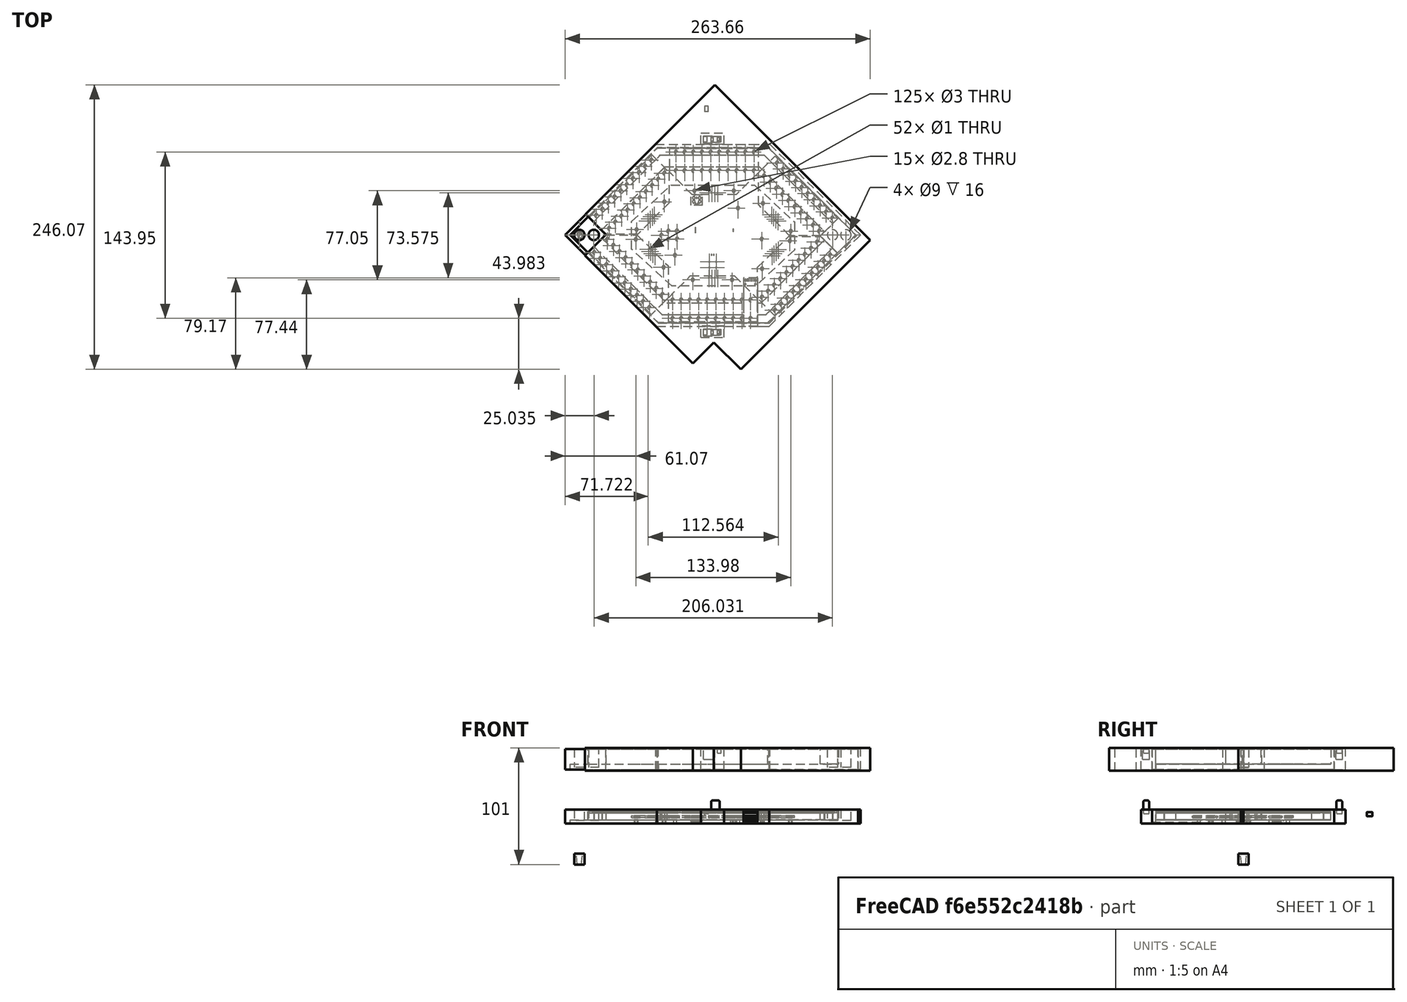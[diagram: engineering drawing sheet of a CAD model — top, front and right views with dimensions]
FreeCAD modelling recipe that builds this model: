
FCSTD DOCUMENT  (FreeCAD 1.0R39109 (Git))
Label: CribbageCase
License: All rights reserved
LicenseURL: https://en.wikipedia.org/wiki/All_rights_reserved
objects: Part::Box×49, Part::Cylinder×25, Part::MultiFuse×12, Part::Cut×8, Part::Feature×7, App::Part×3, Part::Fillet×2, Assembly::JointGroup×1, Mesh::Feature×1, Assembly::AssemblyObject×1, Part::Cone×1
note: 104 computed .brp shape members not serialized (recipe doc carries the construction recipe); baked Part::Feature solids carry a one-line shape summary decoded from their .brp

FEATURE [Assembly::JointGroup] Joints
FEATURE [Part::Feature] Part__Feature  label="MainBoard_PCB"
  shape: bbox 140.8 x 87.5 x 1.6 mm, 105 faces (baked)
FEATURE [Part::Cylinder] Cylinder  label="Screw00"
  Angle = 360
  AttacherType = Attacher::AttachEngine3D
  FirstAngle = 0
  Height = 20
  Placement = pos=(127.1,-56.28,-5) rot=(0,0,1;0rad)
  Radius = 1.4
  SecondAngle = 0
FEATURE [Part::Cylinder] Cylinder001  label="Screw01"
  Angle = 360
  AttacherType = Attacher::AttachEngine3D
  FirstAngle = 0
  Height = 20
  Placement = pos=(161.1,-56.28,-5) rot=(0,0,1;0rad)
  Radius = 1.4
  SecondAngle = 0
FEATURE [Part::Cylinder] Cylinder002  label="Screw03"
  Angle = 360
  AttacherType = Attacher::AttachEngine3D
  FirstAngle = 0
  Height = 20
  Placement = pos=(125.6,-133.33,-5) rot=(0,0,1;0rad)
  Radius = 1.4
  SecondAngle = 0
FEATURE [Part::Cylinder] Cylinder003  label="Screw04"
  Angle = 360
  AttacherType = Attacher::AttachEngine3D
  FirstAngle = 0
  Height = 20
  Placement = pos=(159.6,-133.33,-5) rot=(0,0,1;0rad)
  Radius = 1.4
  SecondAngle = 0
FEATURE [Part::Cylinder] Cylinder004  label="Screw08"
  Angle = 360
  AttacherType = Attacher::AttachEngine3D
  FirstAngle = 0
  Height = 20
  Placement = pos=(100.41,-122.46,-5) rot=(0,0,1;0rad)
  Radius = 1.4
  SecondAngle = 0
FEATURE [Part::Cylinder] Cylinder005  label="Screw02"
  Angle = 360
  AttacherType = Attacher::AttachEngine3D
  FirstAngle = 0
  Height = 20
  Placement = pos=(76.36,-98.41,-5) rot=(0,0,1;0rad)
  Radius = 1.4
  SecondAngle = 0
FEATURE [Part::Cylinder] Cylinder006  label="Screw05"
  Angle = 360
  AttacherType = Attacher::AttachEngine3D
  FirstAngle = 0
  Height = 20
  Placement = pos=(77.02,-89.89,-5) rot=(0,0,1;0rad)
  Radius = 1.4
  SecondAngle = 0
FEATURE [Part::Cylinder] Cylinder007  label="Screw06"
  Angle = 360
  AttacherType = Attacher::AttachEngine3D
  FirstAngle = 0
  Height = 20
  Placement = pos=(210.34,-91.24,-5) rot=(0,0,1;0rad)
  Radius = 1.4
  SecondAngle = 0
FEATURE [Part::Cylinder] Cylinder008  label="Screw07"
  Angle = 360
  AttacherType = Attacher::AttachEngine3D
  FirstAngle = 0
  Height = 20
  Placement = pos=(209.56,-99.67,-5) rot=(0,0,1;0rad)
  Radius = 1.4
  SecondAngle = 0
FEATURE [Part::Cylinder] Cylinder009  label="Screw09"
  Angle = 360
  AttacherType = Attacher::AttachEngine3D
  FirstAngle = 0
  Height = 20
  Placement = pos=(185.52,-123.71,-5) rot=(0,0,1;0rad)
  Radius = 1.4
  SecondAngle = 0
FEATURE [Part::Cylinder] Cylinder010  label="Screw11"
  Angle = 360
  AttacherType = Attacher::AttachEngine3D
  FirstAngle = 0
  Height = 20
  Placement = pos=(186.29,-67.2,-5) rot=(0,0,1;0rad)
  Radius = 1.4
  SecondAngle = 0
FEATURE [Part::Cylinder] Cylinder011  label="Screw10"
  Angle = 360
  AttacherType = Attacher::AttachEngine3D
  FirstAngle = 0
  Height = 20
  Placement = pos=(101.06,-65.84,-5) rot=(0,0,1;0rad)
  Radius = 1.4
  SecondAngle = 0
FEATURE [Part::Cylinder] Cylinder012  label="Screw12"
  Angle = 360
  AttacherType = Attacher::AttachEngine3D
  FirstAngle = 0
  Height = 20
  Placement = pos=(110.25,-112.03,-5) rot=(0,0,1;0rad)
  Radius = 1.4
  SecondAngle = 0
FEATURE [Part::Cylinder] Cylinder013  label="Screw14"
  Angle = 360
  AttacherType = Attacher::AttachEngine3D
  FirstAngle = 0
  Height = 20
  Placement = pos=(185.25,-98.03,-5) rot=(0,0,1;0rad)
  Radius = 1.4
  SecondAngle = 0
FEATURE [Part::Cylinder] Cylinder014  label="Screw13"
  Angle = 360
  AttacherType = Attacher::AttachEngine3D
  FirstAngle = 0
  Height = 20
  Placement = pos=(164.75,-71.28,-5) rot=(0,0,1;0rad)
  Radius = 1.4
  SecondAngle = 0
FEATURE [Part::Box] Box  label="USBCutout"
  AttacherType = Attacher::AttachEngine3D
  Height = 14.5
  Length = 12
  Placement = pos=(181.6,-131.77,-4) rot=(0,0,1;3.14159rad)
  Width = 45
FEATURE [Part::Box] Box001  label="JtagCutout"
  AttacherType = Attacher::AttachEngine3D
  Height = 3
  Length = 10
  Placement = pos=(124,-69,-3) rot=(0,0,1;0rad)
  Width = 9
FEATURE [Part::Feature] Part__Feature007  label="SensorBoard_0"
  Placement = pos=(-50.6,142.4,4) rot=(0,0,1;5.49779rad)
  shape: bbox 68.94 x 68.59 x 1.6 mm, 40 faces (baked)
FEATURE [Part::Feature] Part__Feature008  label="SensorBoard_1"
  Placement = pos=(201.1,198.225,4) rot=(0,0,1;4.71239rad)
  shape: bbox 76.5 x 40 x 1.6 mm, 40 faces (baked)
FEATURE [Part::Feature] Part__Feature009  label="SensorBoard_2"
  Placement = pos=(-131.9,-250.08,4) rot=(0,0,1;0.785398rad)
  shape: bbox 68.59 x 68.94 x 1.6 mm, 40 faces (baked)
FEATURE [Part::Feature] Part__Feature010  label="SensorBoard_3"
  Placement = pos=(85.6,-387.85,4) rot=(0,0,1;1.5708rad)
  shape: bbox 76.5 x 40 x 1.6 mm, 40 faces (baked)
FEATURE [Part::Feature] Part__Feature011  label="SensorBoard_4"
  Placement = pos=(337.2,-331.95,4) rot=(0,0,1;2.35619rad)
  shape: bbox 68.94 x 68.59 x 1.6 mm, 40 faces (baked)
FEATURE [Part::Feature] Part__Feature012  label="SensorBoard_5"
  Placement = pos=(418.58,60.44,4) rot=(0,0,1;3.92699rad)
  shape: bbox 68.59 x 68.94 x 1.6 mm, 40 faces (baked)
FEATURE [App::Part] MainBoard_1  label="Boards"
  Group = -> [Part__Feature,Part__Feature007,Part__Feature008,Part__Feature009,Part__Feature010,Part__Feature011,Part__Feature012]
  Origin = -> Origin001
FEATURE [Part::Box] Box002  label="Baseplate_0"
  AttacherType = Attacher::AttachEngine3D
  Height = 3
  Length = 140.75
  Placement = pos=(72.7,-138.81,-5) rot=(0,0,1;0rad)
  Width = 87.5
FEATURE [Part::Box] Box003  label="Baseplate_001"
  AttacherType = Attacher::AttachEngine3D
  Height = 3
  Length = 107.75
  Placement = pos=(19.53,-94.432,-5) rot=(0,0,1;5.49779rad)
  Width = 106.5
FEATURE [Part::Box] Box004  label="Baseplate_002"
  AttacherType = Attacher::AttachEngine3D
  Height = 3
  Length = 106.75
  Placement = pos=(116.44,-95.14,-5) rot=(0,0,1;5.49779rad)
  Width = 106.5
FEATURE [Part::Box] Box005  label="Baseplate_003"
  AttacherType = Attacher::AttachEngine3D
  Height = 3
  Length = 96.2
  Placement = pos=(95.72,-170.62,-5) rot=(0,0,1;0rad)
  Width = 75
FEATURE [Part::Box] Box006  label="Corner0"
  AttacherType = Attacher::AttachEngine3D
  Height = 9
  Length = 21.9
  Placement = pos=(19.5277,-94.4341,-2) rot=(0,0,1;5.49779rad)
  Width = 22.3
FEATURE [Part::Box] Box007  label="Edge00"
  AttacherType = Attacher::AttachEngine3D
  Height = 12
  Length = 3
  Placement = pos=(17.4063,-92.3128,-4.99) rot=(0,0,1;5.49779rad)
  Width = 107.685
FEATURE [Part::Box] Box008  label="Corner001"
  AttacherType = Attacher::AttachEngine3D
  Height = 9
  Length = 22
  Placement = pos=(267.227,-95.3109,-2) rot=(0,0,-1;3.92699rad)
  Width = 22.2
FEATURE [Part::Box] Box009  label="Support0"
  AttacherType = Attacher::AttachEngine3D
  Height = 6.4
  Length = 10
  Placement = pos=(182.092,-156.207,-2) rot=(0,0,1;5.49779rad)
  Width = 82
FEATURE [Part::Box] Box010  label="Support1"
  AttacherType = Attacher::AttachEngine3D
  Height = 6.4
  Length = 10
  Placement = pos=(98.7721,-153.45,-2) rot=(0,0,-1;1.5708rad)
  Width = 90.4
FEATURE [Part::Box] Box011  label="Support2"
  AttacherType = Attacher::AttachEngine3D
  Height = 6.4
  Length = 85
  Placement = pos=(180.232,-32.4421,-2) rot=(0,0,1;5.49779rad)
  Width = 10
FEATURE [Part::Box] Box012  label="Support3"
  AttacherType = Attacher::AttachEngine3D
  Height = 6.4
  Length = 10
  Placement = pos=(97.5326,-25.4286,-2) rot=(0,0,-1;1.5708rad)
  Width = 89.8
FEATURE [Part::Box] Box013  label="Support4"
  AttacherType = Attacher::AttachEngine3D
  Height = 6.4
  Length = 10
  Placement = pos=(46.4275,-96.8312,-2) rot=(0,0,1;3.92699rad)
  Width = 84
FEATURE [Part::Box] Box014  label="Support5"
  AttacherType = Attacher::AttachEngine3D
  Height = 6.4
  Length = 10
  Placement = pos=(39.2701,-83.7002,-2) rot=(0,0,1;5.49779rad)
  Width = 82.5
FEATURE [Part::Box] Box015  label="Edge001"
  AttacherType = Attacher::AttachEngine3D
  Height = 12
  Length = 3
  Placement = pos=(17.4063,-92.3128,-4.99) rot=(0,0,-1;2.35619rad)
  Width = 112
FEATURE [Part::Box] Box016  label="Edge002"
  AttacherType = Attacher::AttachEngine3D
  Height = 12
  Length = 3
  Placement = pos=(93.552,-16.1678,-4.99) rot=(0,0,-1;1.5708rad)
  Width = 98.75
FEATURE [Part::Box] Box017  label="Edge003"
  AttacherType = Attacher::AttachEngine3D
  Height = 12
  Length = 3
  Placement = pos=(94.492,-170.584,-4.99) rot=(0,0,-1;1.5708rad)
  Width = 97.2
FEATURE [Part::Box] Box018  label="Edge004"
  AttacherType = Attacher::AttachEngine3D
  Height = 12
  Length = 3
  Placement = pos=(189.569,-171.473,-4.99) rot=(0,0,-1;0.785398rad)
  Width = 109
FEATURE [Part::Box] Box019  label="Edge005"
  AttacherType = Attacher::AttachEngine3D
  Height = 12
  Length = 3
  Placement = pos=(192.298,-16.164,-4.99) rot=(0,0,1;3.92699rad)
  Width = 110.9
FEATURE [Part::Box] Box020  label="Baseplate_004"
  AttacherType = Attacher::AttachEngine3D
  Height = 3
  Length = 97.2
  Placement = pos=(94.85,-94.15,-5) rot=(0,0,1;0rad)
  Width = 75
FEATURE [App::Part] Part  label="BottomPlastics"
  Origin = -> Origin002
FEATURE [App::Part] Part001  label="TopPlastics"
  Origin = -> Origin003
FEATURE [Part::Box] Box021  label="Baseplate_005"
  AttacherType = Attacher::AttachEngine3D
  Height = 5
  Length = 97.2
  Placement = pos=(94.85,-94.15,-5) rot=(0,0,1;0rad)
  Width = 75
FEATURE [Part::Box] Box022  label="Baseplate_006"
  AttacherType = Attacher::AttachEngine3D
  Height = 5
  Length = 107.75
  Placement = pos=(19.53,-94.432,-5) rot=(0,0,1;5.49779rad)
  Width = 106.5
FEATURE [Part::Box] Box023  label="Baseplate_007"
  AttacherType = Attacher::AttachEngine3D
  Height = 5
  Length = 140.75
  Placement = pos=(72.7,-138.81,-5) rot=(0,0,1;0rad)
  Width = 87.5
FEATURE [Part::Box] Box024  label="Baseplate_008"
  AttacherType = Attacher::AttachEngine3D
  Height = 5
  Length = 106.75
  Placement = pos=(116.44,-95.14,-5) rot=(0,0,1;5.49779rad)
  Width = 106.5
FEATURE [Part::Box] Box025  label="Baseplate_009"
  AttacherType = Attacher::AttachEngine3D
  Height = 5
  Length = 96.2
  Placement = pos=(95.72,-170.62,-5) rot=(0,0,1;0rad)
  Width = 75
FEATURE [Part::Box] Box026  label="Edge006"
  AttacherType = Attacher::AttachEngine3D
  Height = 18
  Length = 3
  Placement = pos=(17.4063,-92.3128,-4.99) rot=(0,0,1;5.49779rad)
  Width = 107.685
FEATURE [Part::Box] Box027  label="Edge007"
  AttacherType = Attacher::AttachEngine3D
  Height = 18
  Length = 3
  Placement = pos=(17.4063,-92.3128,-4.99) rot=(0,0,-1;2.35619rad)
  Width = 112
FEATURE [Part::Box] Box028  label="Edge008"
  AttacherType = Attacher::AttachEngine3D
  Height = 18
  Length = 3
  Placement = pos=(93.552,-16.1678,-4.99) rot=(0,0,-1;1.5708rad)
  Width = 98.75
FEATURE [Part::Box] Box029  label="Edge009"
  AttacherType = Attacher::AttachEngine3D
  Height = 18
  Length = 3
  Placement = pos=(94.492,-170.584,-4.99) rot=(0,0,-1;1.5708rad)
  Width = 97.2
FEATURE [Part::Box] Box030  label="Edge010"
  AttacherType = Attacher::AttachEngine3D
  Height = 18
  Length = 3
  Placement = pos=(189.569,-171.473,-4.99) rot=(0,0,-1;0.785398rad)
  Width = 109
FEATURE [Part::Box] Box031  label="Edge011"
  AttacherType = Attacher::AttachEngine3D
  Height = 18
  Length = 3
  Placement = pos=(192.298,-16.164,-4.99) rot=(0,0,1;3.92699rad)
  Width = 110.9
FEATURE [Part::Box] Box032  label="Corner002"
  AttacherType = Attacher::AttachEngine3D
  Height = 13
  Length = 21.9
  Placement = pos=(19.5277,-94.4341,0) rot=(0,0,1;5.49779rad)
  Width = 22.3
FEATURE [Part::Box] Box033  label="Corner003"
  AttacherType = Attacher::AttachEngine3D
  Height = 13
  Length = 22
  Placement = pos=(267.227,-95.3109,0) rot=(0,0,-1;3.92699rad)
  Width = 22.2
FEATURE [Part::MultiFuse] Fusion002
  Placement = pos=(0,0,46.5) rot=(0,0,1;0rad)
  Shapes = -> [Box021,Box022,Box023,Box024,Box025,Box026,Box027,Box028,Box029,Box030,Box031,Box032,Box033]
FEATURE [Mesh::Feature] CribbagePeg_Fusion004  label="CribbagePeg-Fusion004"
  Placement = pos=(70.5,-134,74) rot=(0,0,1;0rad)
FEATURE [Part::Cylinder] Cylinder015  label="Cylinder"
  Angle = 360
  AttacherType = Attacher::AttachEngine3D
  FirstAngle = 0
  Height = 25
  Placement = pos=(258,-94.5,13) rot=(0,0,1;0rad)
  Radius = 4.5
  SecondAngle = 0
FEATURE [Part::Cylinder] Cylinder019
  Angle = 360
  AttacherType = Attacher::AttachEngine3D
  FirstAngle = 0
  Height = 25
  Placement = pos=(27.5,-94.5,13) rot=(0,0,1;0rad)
  Radius = 4.5
  SecondAngle = 0
FEATURE [Part::Cylinder] Cylinder020
  Angle = 360
  AttacherType = Attacher::AttachEngine3D
  FirstAngle = 0
  Height = 25
  Placement = pos=(246.5,-94.5,13) rot=(0,0,1;0rad)
  Radius = 4.5
  SecondAngle = 0
FEATURE [Part::Cylinder] Cylinder021
  Angle = 360
  AttacherType = Attacher::AttachEngine3D
  FirstAngle = 0
  Height = 25
  Placement = pos=(40,-94.5,13) rot=(0,0,1;0rad)
  Radius = 4.5
  SecondAngle = 0
FEATURE [Part::Cylinder] Cylinder022
  Angle = 360
  AttacherType = Attacher::AttachEngine3D
  FirstAngle = 0
  Height = 25
  Placement = pos=(258,-94.5,13) rot=(0,0,1;0rad)
  Radius = 4.5
  SecondAngle = 0
FEATURE [Part::Cylinder] Cylinder023
  Angle = 360
  AttacherType = Attacher::AttachEngine3D
  FirstAngle = 0
  Height = 25
  Placement = pos=(27.5,-94.5,13) rot=(0,0,1;0rad)
  Radius = 4.5
  SecondAngle = 0
FEATURE [Part::Cylinder] Cylinder024
  Angle = 360
  AttacherType = Attacher::AttachEngine3D
  FirstAngle = 0
  Height = 25
  Placement = pos=(246.5,-94.5,13) rot=(0,0,1;0rad)
  Radius = 4.5
  SecondAngle = 0
FEATURE [Part::Cylinder] Cylinder025
  Angle = 360
  AttacherType = Attacher::AttachEngine3D
  FirstAngle = 0
  Height = 25
  Placement = pos=(40,-94.5,13) rot=(0,0,1;0rad)
  Radius = 4.5
  SecondAngle = 0
FEATURE [Part::MultiFuse] Fusion
  Placement = pos=(0,0,-15.5) rot=(0,0,1;0rad)
  Shapes = -> [Cylinder015,Cylinder019,Cylinder020,Cylinder021]
FEATURE [Part::MultiFuse] Fusion003
  Placement = pos=(0,0,30.5) rot=(0,0,1;0rad)
  Shapes = -> [Cylinder022,Cylinder023,Cylinder024,Cylinder025]
FEATURE [Part::MultiFuse] Fusion004
  Shapes = -> [Cylinder014,Cylinder,Cylinder001,Cylinder002,Cylinder003,Cylinder004,Cylinder005,Cylinder006,Cylinder007,Cylinder008,Cylinder009,Cylinder010,Cylinder011,Cylinder012,Cylinder013,Box,Box001,Fusion]
FEATURE [Part::MultiFuse] Fusion005
  Shapes = -> [Box015,Box018,Box019,Box016,Box017,Box020,Box002,Box003,Box004,Box005,Box006,Box008,Box009,Box007,Box010,Box011,Box012,Box013,Box014]
FEATURE [Part::Cut] Cut  label="TopHousing"
  Base = -> Fusion002
  Tool = -> Fusion003
FEATURE [Part::Cut] Cut001  label="BottomHousing"
  Base = -> Fusion005
  Tool = -> Fusion004
FEATURE [Part::Box] Box034  label="Cube"
  AttacherType = Attacher::AttachEngine3D
  Height = 12
  Length = 20
  Placement = pos=(132.5,-16.25,-5) rot=(0,0,1;0rad)
  Width = 10
FEATURE [Part::Cylinder] Cylinder026  label="Magnet"
  Angle = 360
  AttacherType = Attacher::AttachEngine3D
  FirstAngle = 0
  Height = 4.85
  Placement = pos=(137.5,12,3) rot=(1,0,0;4.71239rad)
  Radius = 1.65
  SecondAngle = 0
FEATURE [Part::Box] Box035  label="Cube001"
  AttacherType = Attacher::AttachEngine3D
  Height = 8
  Length = 7.5
  Placement = pos=(141.5,-14.25,7) rot=(0,0,1;0rad)
  Width = 5
FEATURE [Part::Box] Box036  label="Cube002"
  AttacherType = Attacher::AttachEngine3D
  Height = 18
  Length = 20
  Placement = pos=(132.5,-16.25,41.5) rot=(0,0,1;0rad)
  Width = 10
FEATURE [Part::Box] Box037  label="Cube003"
  AttacherType = Attacher::AttachEngine3D
  Height = 9
  Length = 8.5
  Placement = pos=(135,-14.75,50.5) rot=(0,0,1;0rad)
  Width = 6
FEATURE [Part::Fillet] Fillet
  Base = -> Box035
  EdgeLinks = -> Box035 [Edge2,Edge6,Edge10,Edge12]
  Edges = 4 edges r=1.5: [Edge2,Edge6,Edge10,Edge12]
FEATURE [Part::Box] Box038  label="Magnet001"
  AttacherType = Attacher::AttachEngine3D
  Height = 3.5
  Length = 3.2
  Placement = pos=(135,-14,3.5) rot=(0,0,1;0rad)
  Width = 4.85
FEATURE [Part::Box] Box039  label="Magnet002"
  AttacherType = Attacher::AttachEngine3D
  Height = 3.5
  Length = 3.2
  Placement = pos=(147,-14,56) rot=(0,0,1;0rad)
  Width = 4.85
FEATURE [Part::MultiFuse] Fusion006
  Shapes = -> [Box037,Box039]
FEATURE [Part::Cut] Cut002
  Base = -> Box036
  Tool = -> Fusion006
FEATURE [Part::Cut] Cut003
  Base = -> Box034
  Tool = -> Box038
FEATURE [Part::MultiFuse] Fusion007
  Shapes = -> [Cut003,Fillet]
FEATURE [Part::Box] Box040  label="Cube004"
  AttacherType = Attacher::AttachEngine3D
  Height = 18
  Length = 20
  Placement = pos=(132.5,-16.25,41.5) rot=(0,0,1;0rad)
  Width = 10
FEATURE [Part::Box] Box041  label="Cube005"
  AttacherType = Attacher::AttachEngine3D
  Height = 9
  Length = 8.5
  Placement = pos=(135,-14.75,50.5) rot=(0,0,1;0rad)
  Width = 6
FEATURE [Part::Box] Box042  label="Magnet003"
  AttacherType = Attacher::AttachEngine3D
  Height = 3.5
  Length = 3.2
  Placement = pos=(147,-14,56) rot=(0,0,1;0rad)
  Width = 4.85
FEATURE [Part::MultiFuse] Fusion008
  Shapes = -> [Box041,Box042]
FEATURE [Part::Cut] Cut004
  Base = -> Box040
  Placement = pos=(0,-167,0) rot=(0,0,1;0rad)
  Tool = -> Fusion008
FEATURE [Part::Box] Box043  label="Cube006"
  AttacherType = Attacher::AttachEngine3D
  Height = 12
  Length = 20
  Placement = pos=(132.5,-16.25,-5) rot=(0,0,1;0rad)
  Width = 10
FEATURE [Part::Box] Box044  label="Cube007"
  AttacherType = Attacher::AttachEngine3D
  Height = 8
  Length = 7.5
  Placement = pos=(141.5,-14.25,7) rot=(0,0,1;0rad)
  Width = 5
FEATURE [Part::Box] Box045  label="Magnet004"
  AttacherType = Attacher::AttachEngine3D
  Height = 3.5
  Length = 3.2
  Placement = pos=(135,-14,3.5) rot=(0,0,1;0rad)
  Width = 4.85
FEATURE [Part::Cut] Cut005
  Base = -> Box043
  Tool = -> Box045
FEATURE [Part::Fillet] Fillet001
  Base = -> Box044
  EdgeLinks = -> Box044 [Edge2,Edge6,Edge10,Edge12]
  Edges = 4 edges r=1.5: [Edge2,Edge6,Edge10,Edge12]
FEATURE [Part::MultiFuse] Fusion009
  Placement = pos=(0,-167,0) rot=(0,0,1;0rad)
  Shapes = -> [Cut005,Fillet001]
FEATURE [Part::MultiFuse] Fusion010
  Shapes = -> [Cut,Cut002,Cut004]
FEATURE [Part::MultiFuse] Fusion011
  Shapes = -> [Cut001,Fusion007,Fusion009]
FEATURE [Assembly::AssemblyObject] Assembly  label="Cuts"
  Group = -> [Joints,Cylinder021,Fusion004,Fusion,Fillet,Fusion007,Fusion005,Cut005,Cut001,Fillet001,Cut003,Box018,Box019,Box016,Box045,Box017,Box020,Box034,Cylinder,Cylinder001,Cylinder002,Cylinder003,Cylinder004,Cylinder005,Cylinder006,Cylinder007,Cylinder008,Cylinder009,Cylinder010,Cylinder011,Cylinder012,Cylinder013,Cylinder014,Box,Box001,Box002,Box003,Box004,Box005,Box006,Box007,Box008,Box009,Box010,+14 more]
  Origin = -> Origin
  Type = Assembly
FEATURE [Part::Box] Box046  label="Cube008"
  AttacherType = Attacher::AttachEngine3D
  Height = 20
  Length = 190
  Placement = pos=(32.8805,-76.4246,40.5) rot=(0,0,1;5.49779rad)
  Width = 158
FEATURE [Part::Box] Box047  label="Cube009"
  AttacherType = Attacher::AttachEngine3D
  Height = 20
  Length = 26
  Placement = pos=(50.5581,-94.1023,40.5) rot=(0,0,-1;2.35619rad)
  Width = 132
FEATURE [Part::MultiFuse] Fusion012
  Shapes = -> [Box046,Box047]
FEATURE [Part::Cylinder] Cylinder028
  Angle = 360
  AttacherType = Attacher::AttachEngine3D
  FirstAngle = 0
  Height = 16
  Placement = pos=(27.5,-94.5,71) rot=(0,0,1;0rad)
  Radius = 4.4
  SecondAngle = 0
FEATURE [Part::Cone] Cone
  Angle = 360
  AttacherType = Attacher::AttachEngine3D
  Height = 16
  Placement = pos=(27.5,-94.5,71) rot=(0,0,1;0rad)
  Radius1 = 1.75
  Radius2 = 3.5
FEATURE [Part::Cut] Cut006
  Base = -> Cylinder028
  Placement = pos=(0,0,-111.5) rot=(0,0,1;0rad)
  Tool = -> Cone
FEATURE [Part::Box] Box048  label="Cube010"
  AttacherType = Attacher::AttachEngine3D
  Height = 6.5
  Length = 10
  Placement = pos=(22.5,-99.5,-31) rot=(0,0,1;0rad)
  Width = 10
FEATURE [Part::Cut] Cut007
  Base = -> Cut006
  Tool = -> Box048
